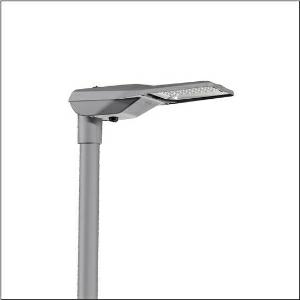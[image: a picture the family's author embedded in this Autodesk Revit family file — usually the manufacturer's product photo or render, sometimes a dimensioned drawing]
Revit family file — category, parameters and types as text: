
# Revit family: streetlight_sl_21_mini___st1_5a_5xe2p33t08hb_306c
name_source: partatom
category: Lighting Fixtures
units: mm (PartAtom-declared; Revit-internal decimal feet)

## family parameters
Cut with Voids When Loaded = No
Host = Face
Light Source = No
Part Type = Normal
Room Calculation Point = No
Round Connector Dimension = Use Diameter
Shared = No

## types (1)
- --- (1 x LED, 8890 lm, 66 W, 3000K)
    Apparent Load = 66 VA
    CIE Flux Codes = 22 53 95 100 100
    Color Rendering = 70
    Color Temperature = 3000K
    Default Elevation = 1800 mm
    Description = Streetlight SL 21 mini, mast luminaire, primary light control with lens, of PMMA, primary optical cover: cover, of toughened safety glass, transparent, light distribution: ST1.5a, light emission: direct distribution, primary light characteristic: asymmetric, installation type: side-entry, post-top, LED, High Power LED, rated luminous flux: 8.890lm, luminous efficacy: 135lm/W, light colour: 730, colour temperature: 3000K, control gear: D4i, control: overheat protection, constant luminous flux control, time-dependent luminous flux control, flexible luminous flux parameterisation, pre-setting: logarithmic dimming characteristic, mains connection: 220..240V, AC, 50/60Hz, start of lifetime: 66W, end of service life: 69W, reduction: 30W, luminaire housing, of diecast aluminium, powder-coated, SITECO metallic grey (DB 702S), corrosivity category C5 high according to DIN EN ISO 12944, please order mast flange separately, inclination adjustable: 0°, 5°, 10°, 15°, sealing non-destructively replaceable, multi-level sealing system, length: 628mm, width: 235mm, height: 110mm, mast flange for spigot size: 42mm (side-entry): 5XC10008XM4, 60/48mm (side-entry/post-top): 5XC10108XM2, 76/60mm (side-entry/post-top): 5XC10108XM1, mounting height: 4..8m, Smart Interface below and above, protection rating (complete): IP66, insulation class (complete): insulation class II (safety insulation), certification: CE, ENEC, ENEC+, VDE, impact resistance: IK10, permissible operating ambient temperature for outdoor applications: -40..+50°C, standard-compliant lighting for roads and squares, packaging unit: 1 piece

Light Distribution: ST1.5a
    Height = 110 mm
    Lamp = 1 x LED
    Lamp Light Flux = 8890 lm
    Lamp Power = 66 W
    Lamp count = 1
    Length = 625 mm
    Luminous efficacy = 135 lm/W
    Manufacturer = Siteco
    ModVariant = No
    Model = 5XE2P33T08HB
    Number of Poles = 1
    OnlyDefault = Yes
    Power Factor = 1
    Product Name = Streetlight SL 21 mini | ST1.5a
    Product group = mast luminaire | pylon top
    ProductGroupID = 6100
    Protection Class = Protection class II
    Protection Degree = IP 66
    RLX_Detail_Level = 1
    RLX_Emergency_Light_Flux = 0 lm
    RLX_Emergency_Type = 0
    RLX_Emergency_Type_DB = No
    RlxData = <blob elided: 29773 chars, md5=5f647df8>
    Socket = socket
    Standby Power = 0 W
    System Light Flux = 8890 lm
    System Power = 66 W
    Type Comments = factory setting: luminous flux: 100 % | dim-lin: 254 | 670 mA
    Type Image = l_1003514.jpg
    URL = http://relux.com
    VarID = @adj_174977
    Voltage = 0 V
    Weight = 0.00 kg
    Width = 234 mm

## geometry (parser evidence)
native form markers: Blend x4, Sweep x10
no freeform markers — native parametric forms only
